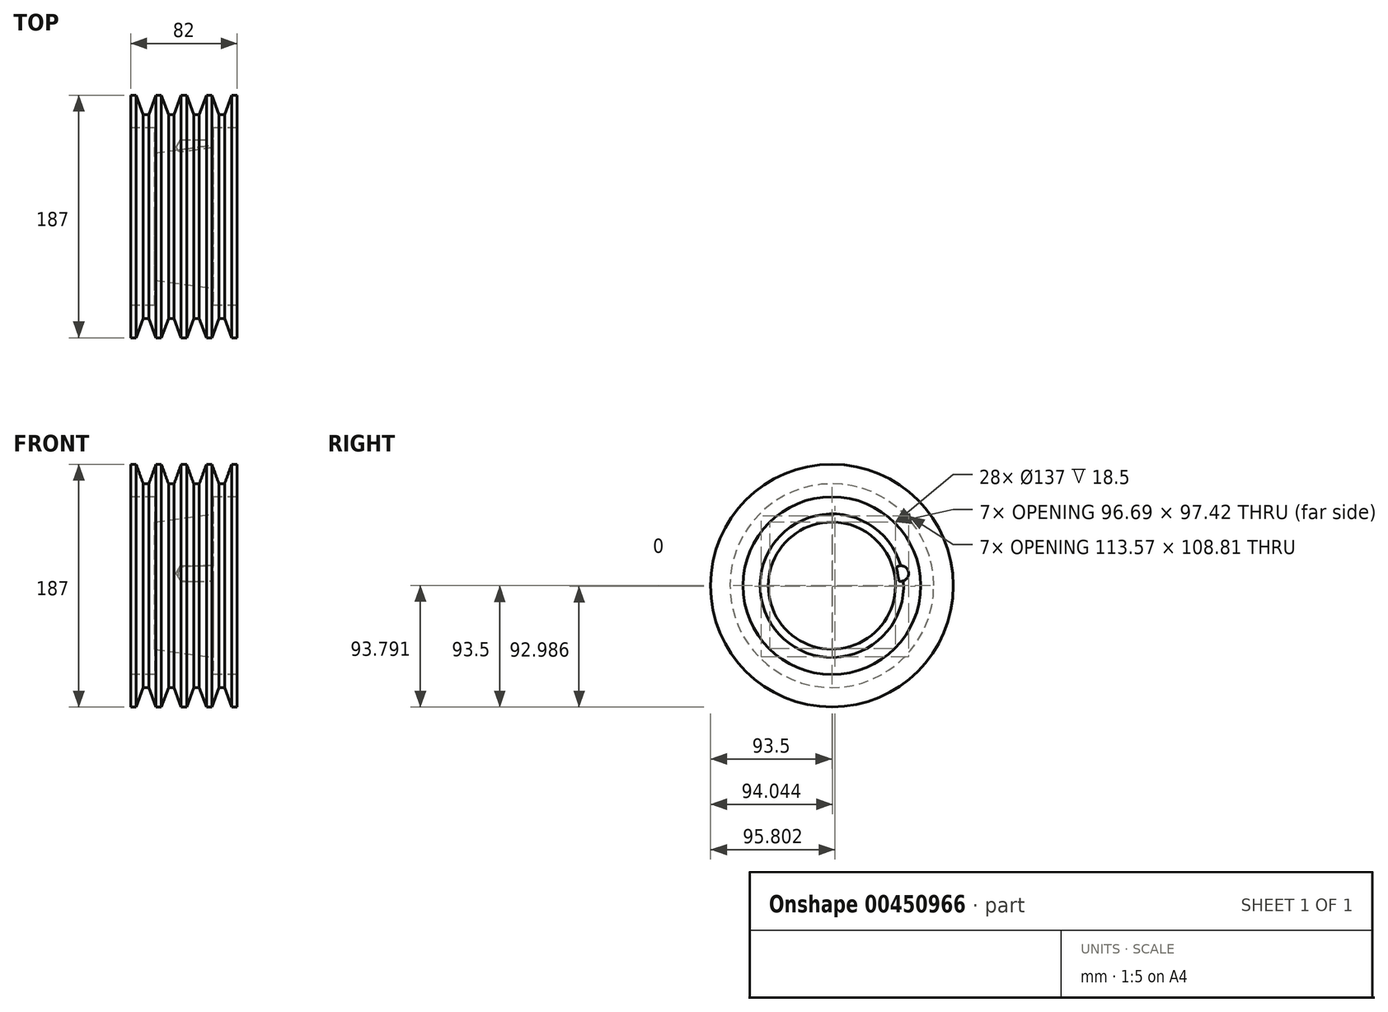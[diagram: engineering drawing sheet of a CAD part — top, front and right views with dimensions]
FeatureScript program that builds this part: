
annotation { "Feature Type Name" : "Feature", "Feature Type Description" : "" }
export const myFeature = defineFeature(function(context is Context, id is Id, definition is map)
    precondition{}
    {
        {
            var Q0;
            Q0=qCreatedBy(makeId("Front.planeOp"),FACE);
            var sketch = newSketch(context, id + "F0", { "sketchPlane" : qUnion([Q0])});
            skLineSegment(sketch, "E0", {"start": v(-22.5, 49) * mm, "end": v(22.5, 55.32) * mm});
            skLineSegment(sketch, "E1", {"start": v(-22.5, 49) * mm, "end": v(-22.5, 68.5) * mm});
            skLineSegment(sketch, "E2", {"start": v(22.5, 55.32) * mm, "end": v(22.5, 68.5) * mm});
            skLineSegment(sketch, "E3", {"start": v(-22.5, 68.5) * mm, "end": v(-41, 68.5) * mm});
            skLineSegment(sketch, "E4", {"start": v(-41, 68.5) * mm, "end": v(-41, 93.5) * mm});
            skLineSegment(sketch, "E5", {"start": v(-41, 93.5) * mm, "end": v(-36.8, 93.5) * mm});
            skLineSegment(sketch, "E6", {"start": v(-31.33, 78.5) * mm, "end": v(-27.01, 78.5) * mm});
            skLineSegment(sketch, "E7", {"start": v(-29.17, 94.23) * mm, "end": v(-29.17, 77.98) * mm, "construction": true});
            skLineSegment(sketch, "E8", {"start": v(-31.33, 78.5) * mm, "end": v(-36.8, 93.5) * mm});
            skLineSegment(sketch, "E9.MirrorCS", {"start": v(-27.01, 78.5) * mm, "end": v(-21.55, 93.5) * mm});
            skLineSegment(sketch, "E10.MirrorCS", {"start": v(41, 68.5) * mm, "end": v(41, 93.5) * mm});
            skLineSegment(sketch, "E11.MirrorCS", {"start": v(41, 93.5) * mm, "end": v(36.8, 93.5) * mm});
            skLineSegment(sketch, "E12.MirrorCS", {"start": v(31.33, 78.5) * mm, "end": v(36.8, 93.5) * mm});
            skLineSegment(sketch, "E13.MirrorCS", {"start": v(31.33, 78.5) * mm, "end": v(27.01, 78.5) * mm});
            skLineSegment(sketch, "E14.MirrorCS", {"start": v(27.01, 78.5) * mm, "end": v(21.55, 93.5) * mm});
            skLineSegment(sketch, "E15.MirrorCS", {"start": v(22.5, 68.5) * mm, "end": v(41, 68.5) * mm});
            skLineSegment(sketch, "E16.MirrorCS", {"start": v(-17.34, 93.5) * mm, "end": v(-21.55, 93.5) * mm});
            skLineSegment(sketch, "E17", {"start": v(-19.45, 100.84) * mm, "end": v(-19.45, 81.52) * mm, "construction": true});
            skLineSegment(sketch, "E18.MirrorCS", {"start": v(-11.88, 78.5) * mm, "end": v(-17.34, 93.5) * mm});
            skLineSegment(sketch, "E19.MirrorCS", {"start": v(-7.56, 78.5) * mm, "end": v(-11.88, 78.5) * mm});
            skLineSegment(sketch, "E20.MirrorCS", {"start": v(-7.56, 78.5) * mm, "end": v(-2.1, 93.5) * mm});
            skLineSegment(sketch, "E21.MirrorCS", {"start": v(2.1, 93.5) * mm, "end": v(-2.1, 93.5) * mm});
            skLineSegment(sketch, "E22.MirrorCS", {"start": v(17.34, 93.5) * mm, "end": v(21.55, 93.5) * mm});
            skLineSegment(sketch, "E23.MirrorCS", {"start": v(11.88, 78.5) * mm, "end": v(17.34, 93.5) * mm});
            skLineSegment(sketch, "E24.MirrorCS", {"start": v(7.56, 78.5) * mm, "end": v(11.88, 78.5) * mm});
            skLineSegment(sketch, "E25.MirrorCS", {"start": v(7.56, 78.5) * mm, "end": v(2.1, 93.5) * mm});
            skLineSegment(sketch, "E26", {"start": v(0, 98.38) * mm, "end": v(0, 88.2) * mm, "construction": true});
            skPoint(sketch, "E26.endSnap0", {"position": v(0, 93.5) * mm});
            skLineSegment(sketch, "E27", {"start": v(-9.72, 100.78) * mm, "end": v(-9.72, 71.3) * mm, "construction": true});
            skLineSegment(sketch, "E28", {"start": v(-66.56, 0) * mm, "end": v(57.96, 0) * mm, "construction": true});
            skSolve(sketch);
        }
        {
            var Q0;
            Q0 = qSketchRegion(id + "F0", true);
            var Q1;
            Q1=sQuery(id+"F0.wireOp",EDGE,"E28");
            revolve(context, id + "F1", {"entities" : qUnion([Q0]), "axis" : qUnion([Q1]), "revolveType" : RevolveType.FULL});
        }
        {
            var Q0;
            Q0=makeQuery(id+"F1.opRevolve","SWEPT_FACE",FACE,{"disambiguationData":[OSD([sQuery(id+"F0.wireOp",EDGE,"E2")])]});
            var sketch = newSketch(context, id + "F2", { "sketchPlane" : qUnion([Q0])});
            skCircle(sketch, "E29", {"center": v(0, 0) * mm, "radius": 54 * mm, "construction": true});
            skLineSegment(sketch, "E30", {"start": v(0, 0) * mm, "end": v(101.75, 17.94) * mm, "construction": true});
            skCircle(sketch, "E31", {"center": v(53.18, 9.38) * mm, "radius": 6.25 * mm});
            skSolve(sketch);
        }
        {
            var Q0;
            Q0=makeQuery(id+"F1.opRevolve","SWEPT_FACE",FACE,{"disambiguationData":[OSD([sQuery(id+"F0.wireOp",EDGE,"E2")])]});
            var sketch = newSketch(context, id + "F3", { "sketchPlane" : qUnion([Q0])});
            skPoint(sketch, "E32", {"position": v(53.18, 9.38) * mm});
            skSolve(sketch);
        }
        {
            var Q0;
            Q0=sQuery(id+"F3.wireOp",VERTEX,"E32");
            var Q1;
            Q1=makeQuery(id+"F1.opRevolve","SWEPT_BODY",BODY,{"disambiguationData":[OSD([sQuery(id+"F0.wireOp",EDGE,"E0"),sQuery(id+"F0.wireOp",EDGE,"E1"),sQuery(id+"F0.wireOp",EDGE,"E2"),sQuery(id+"F0.wireOp",EDGE,"E3"),sQuery(id+"F0.wireOp",EDGE,"E4"),sQuery(id+"F0.wireOp",EDGE,"E5"),sQuery(id+"F0.wireOp",EDGE,"E6"),sQuery(id+"F0.wireOp",EDGE,"E8"),sQuery(id+"F0.wireOp",EDGE,"E9.MirrorCS"),sQuery(id+"F0.wireOp",EDGE,"E10.MirrorCS"),sQuery(id+"F0.wireOp",EDGE,"E11.MirrorCS"),sQuery(id+"F0.wireOp",EDGE,"E12.MirrorCS"),sQuery(id+"F0.wireOp",EDGE,"E13.MirrorCS"),sQuery(id+"F0.wireOp",EDGE,"E14.MirrorCS"),sQuery(id+"F0.wireOp",EDGE,"E15.MirrorCS"),sQuery(id+"F0.wireOp",EDGE,"E16.MirrorCS"),sQuery(id+"F0.wireOp",EDGE,"E18.MirrorCS"),sQuery(id+"F0.wireOp",EDGE,"E19.MirrorCS"),sQuery(id+"F0.wireOp",EDGE,"E20.MirrorCS"),sQuery(id+"F0.wireOp",EDGE,"E21.MirrorCS"),sQuery(id+"F0.wireOp",EDGE,"E22.MirrorCS"),sQuery(id+"F0.wireOp",EDGE,"E23.MirrorCS"),sQuery(id+"F0.wireOp",EDGE,"E24.MirrorCS"),sQuery(id+"F0.wireOp",EDGE,"E25.MirrorCS")])]});
            hole(context, id + "F4", {"style" : HoleStyle.SIMPLE, "endStyle" : HoleEndStyle.BLIND, "holeDiameter" : 12 * mm, "holeDepth" : 25 * mm, "isTappedThrough" : true, "tappedDepth" : 19.75 * mm, "tapClearance" : 3, "startFromSketch" : true, "locations" : qUnion([Q0]), "scope" : qUnion([Q1])});
        }
    });
